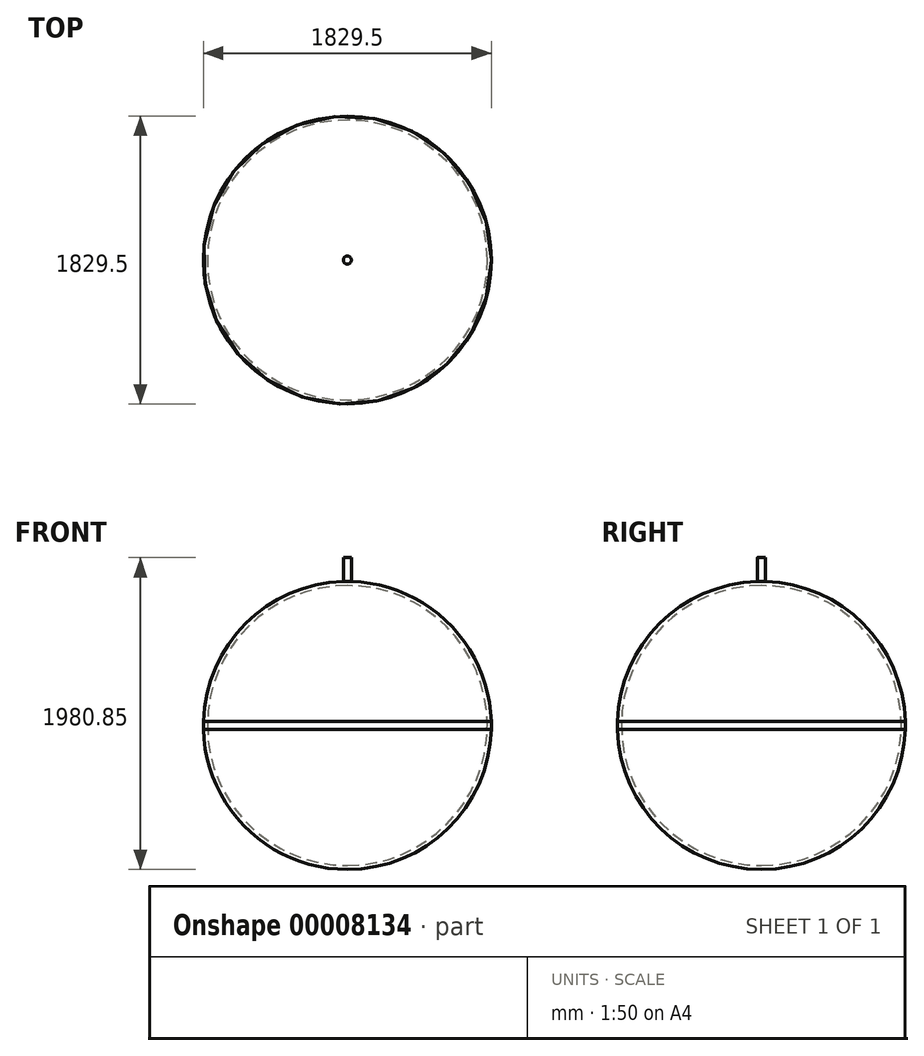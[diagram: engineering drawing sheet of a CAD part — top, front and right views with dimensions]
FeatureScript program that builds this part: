
annotation { "Feature Type Name" : "Feature", "Feature Type Description" : "" }
export const myFeature = defineFeature(function(context is Context, id is Id, definition is map)
    precondition{}
    {
        {
            var Q0;
            Q0=qCreatedBy(makeId("Front.planeOp"),FACE);
            var sketch = newSketch(context, id + "F0", { "sketchPlane" : qUnion([Q0])});
            skArc(sketch, "E0", {"start": v(-25.4, 914.05) * mm, "mid": v(-646.58, 646.58) * mm, "end": v(-914.05, 25.4) * mm});
            skArc(sketch, "E1", {"start": v(0, 889) * mm, "mid": v(-889, 0) * mm, "end": v(0, -889) * mm});
            skLineSegment(sketch, "E2", {"start": v(0, 914.4) * mm, "end": v(0, -914.4) * mm, "construction": true});
            skLineSegment(sketch, "E3", {"start": v(0, 914.4) * mm, "end": v(0, 889) * mm});
            skLineSegment(sketch, "E4", {"start": v(0, -889) * mm, "end": v(0, -914.4) * mm});
            skArc(sketch, "E5.trimOffspring", {"start": v(-914.05, -25.4) * mm, "mid": v(-637.53, -655.5) * mm, "end": v(0, -914.4) * mm});
            skArc(sketch, "E6", {"start": v(-914.05, 25.4) * mm, "mid": v(-914.75, 0) * mm, "end": v(-914.05, -25.4) * mm});
            skLineSegment(sketch, "E7", {"start": v(-25.4, 914.05) * mm, "end": v(-25.4, 1066.45) * mm});
            skLineSegment(sketch, "E8", {"start": v(-25.4, 1066.45) * mm, "end": v(0, 1066.45) * mm});
            skLineSegment(sketch, "E9", {"start": v(0, 1066.45) * mm, "end": v(0, 914.4) * mm});
            skSolve(sketch);
        }
        {
            var Q0;
            Q0=makeQuery(id+"F0.imprint","IMPRINT",FACE,{"disambiguationData":[TD([[makeQuery(id+"F0.imprint","IMPRINT",EDGE,{"derivedFrom":sQuery(id+"F0.wireOp",EDGE,"E0")}),1.0]])]});
            var Q1;
            Q1=sQuery(id+"F0.wireOp",EDGE,"E2");
            revolve(context, id + "F1", {"entities" : qUnion([Q0]), "axis" : qUnion([Q1]), "revolveType" : RevolveType.FULL});
        }
    });
